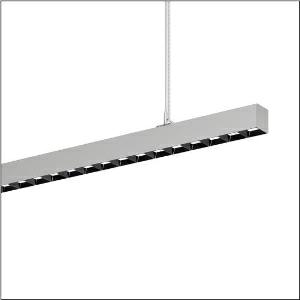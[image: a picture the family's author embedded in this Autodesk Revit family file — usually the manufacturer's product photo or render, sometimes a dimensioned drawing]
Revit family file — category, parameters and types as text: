
# Revit family: silica_r__21_51mx31dc4dsb_9913
name_source: partatom
category: Lighting Fixtures
units: mm (PartAtom-declared; Revit-internal decimal feet)

## family parameters
Cut with Voids When Loaded = No
Host = Face
Light Source = No
Part Type = Normal
Room Calculation Point = No
Round Connector Dimension = Use Diameter
Shared = No

## types (1)
- --- (1 x LED, 18230 lm, 105.9 W, 4000K)
    Apparent Load = 106 VA
    CIE Flux Codes = 87 99 100 59 100
    Color Rendering = 80
    Color Temperature = 4000K
    Default Elevation = 1800 mm
    Description = Silica® 21, office luminaire, primary light control with darklight reflector, of PMMA, black, CAT 2 (L<= 3000cd/m²), light emission: direct/indirect distribution, primary light characteristic: symmetric, installation type: suspended mounting, LED, rated luminous flux: 18.230lm, luminous efficacy: 172lm/W, light colour: 840, colour temperature: 4000K, with terminal, 3+2-pole, max. 2.5mm², mains connection: 220..240V, AC, 50/60Hz, rated input power: 105.9W, luminaire housing, of aluminium, metallic grey (RAL 9006), length: 3.004mm, width: 53mm, height: 53mm, protection rating (complete): IP20, insulation class (complete): insulation class I (protective earthing), certification: CE, permissible operating ambient temperature: 0..+35°C, standard: EN 50419, packaging unit: 1 piece
    Height = 53 mm
    Lamp = 1 x LED
    Lamp Light Flux = 18230 lm
    Lamp Power = 105.9 W
    Lamp count = 1
    Length = 3004 mm
    Luminous efficacy = 172 lm/W
    Manufacturer = Siteco
    ModVariant = No
    Model = 51MX31DC4DSB
    Mounting Place = Ceiling
    Mounting Type = Pendant
    Number of Poles = 1
    OnlyDefault = Yes
    Power Factor = 1
    Product Name = Silica® 21
    Product group = office luminaire | ceiling pendant
    ProductGroupID = 902
    Protection Class = Protection class I
    Protection Degree = IP 20
    RLX_Detail_Level = 1
    RLX_Emergency_Light_Flux = 0 lm
    RLX_Emergency_Type = 0
    RLX_Emergency_Type_DB = No
    RlxData = <blob elided: 65813 chars, md5=467430c6>
    Socket = socket
    Standby Power = 0 W
    System Light Flux = 18230 lm
    System Power = 106 W
    Type Comments = factory setting: luminous flux: 100 % | dim-lin: 254 | 367 mA
    Type Image = l_1297751.jpg
    URL = http://relux.com
    VarID = @adj_051671
    Voltage = 0 V
    Weight = 0.00 kg
    Width = 53 mm

## geometry (parser evidence)
native form markers: Blend x4, Sweep x11
no freeform markers — native parametric forms only
